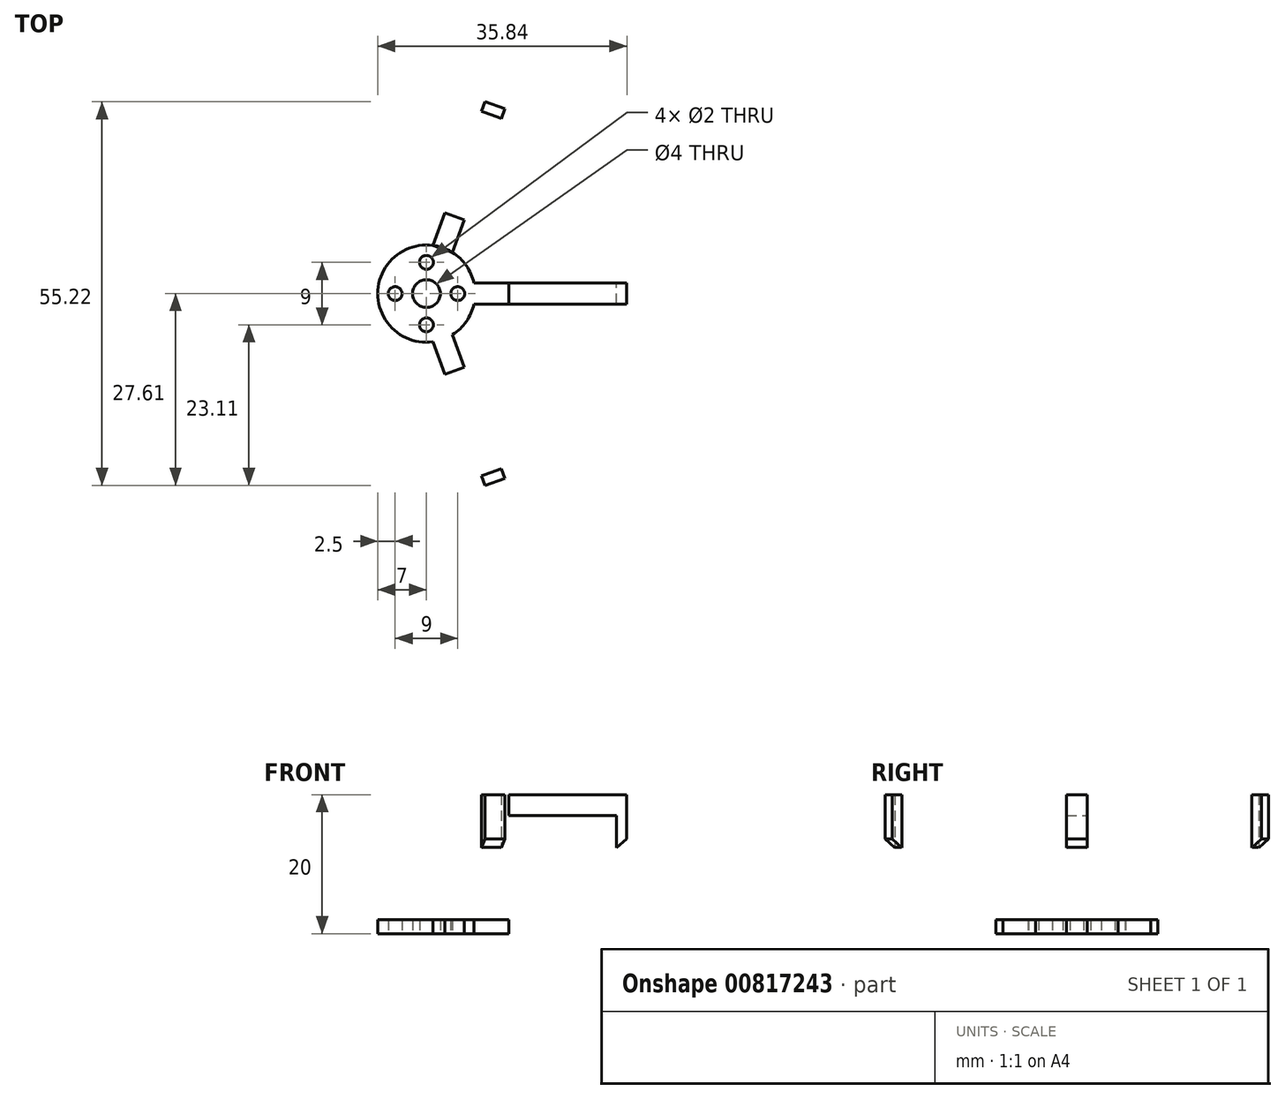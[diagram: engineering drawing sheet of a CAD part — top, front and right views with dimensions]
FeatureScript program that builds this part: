
annotation { "Feature Type Name" : "Feature", "Feature Type Description" : "" }
export const myFeature = defineFeature(function(context is Context, id is Id, definition is map)
    precondition{}
    {
        {
            var Q0;
            Q0=qCreatedBy(makeId("Top.planeOp"),FACE);
            var sketch = newSketch(context, id + "F0", { "sketchPlane" : qUnion([Q0])});
            skCircle(sketch, "E0", {"center": v(0, 0) * mm, "radius": 7 * mm});
            skCircle(sketch, "E1", {"center": v(0, -4.5) * mm, "radius": 1 * mm});
            skCircle(sketch, "E2.1.0", {"center": v(4.5, 0) * mm, "radius": 1 * mm});
            skCircle(sketch, "E2.2.0", {"center": v(0, 4.5) * mm, "radius": 1 * mm});
            skCircle(sketch, "E2.3.0", {"center": v(-4.5, 0) * mm, "radius": 1 * mm});
            skLineSegment(sketch, "E3.bottom", {"start": v(6.84, -1.5) * mm, "end": v(11.84, -1.5) * mm});
            skLineSegment(sketch, "E3.top", {"start": v(6.84, 1.5) * mm, "end": v(11.84, 1.5) * mm});
            skLineSegment(sketch, "E3.left", {"start": v(6.84, -1.5) * mm, "end": v(6.84, 1.5) * mm});
            skLineSegment(sketch, "E3.right", {"start": v(11.84, -1.5) * mm, "end": v(11.84, 1.5) * mm});
            skCircle(sketch, "E4", {"center": v(0, 0) * mm, "radius": 2 * mm});
            skLineSegment(sketch, "E5.1.0", {"start": v(0.93, -6.94) * mm, "end": v(3.75, -5.91) * mm});
            skLineSegment(sketch, "E5.1.1", {"start": v(0.93, -6.94) * mm, "end": v(2.64, -11.64) * mm});
            skLineSegment(sketch, "E5.1.2", {"start": v(3.75, -5.91) * mm, "end": v(5.46, -10.61) * mm});
            skLineSegment(sketch, "E5.1.3", {"start": v(2.64, -11.64) * mm, "end": v(5.46, -10.61) * mm});
            skLineSegment(sketch, "E5.anchor1", {"start": v(0, 0) * mm, "end": v(6.84, -1.5) * mm, "construction": true});
            skLineSegment(sketch, "E5.anchor2", {"start": v(0, 0) * mm, "end": v(0.93, -6.94) * mm, "construction": true});
            skLineSegment(sketch, "E6.MirrorCS", {"start": v(3.75, 5.91) * mm, "end": v(5.46, 10.61) * mm});
            skLineSegment(sketch, "E7.MirrorCS", {"start": v(0.93, 6.94) * mm, "end": v(2.64, 11.64) * mm});
            skLineSegment(sketch, "E8.MirrorCS", {"start": v(0.93, 6.94) * mm, "end": v(3.75, 5.91) * mm});
            skLineSegment(sketch, "E9.MirrorCS", {"start": v(2.64, 11.64) * mm, "end": v(5.46, 10.61) * mm});
            skPoint(sketch, "E10", {"position": v(11.84, 0) * mm});
            skLineSegment(sketch, "E11.bottom", {"start": v(11.84, -1.5) * mm, "end": v(28.84, -1.5) * mm});
            skLineSegment(sketch, "E11.top", {"start": v(11.84, 1.5) * mm, "end": v(28.84, 1.5) * mm});
            skLineSegment(sketch, "E11.right", {"start": v(28.84, -1.5) * mm, "end": v(28.84, 1.5) * mm});
            skLineSegment(sketch, "E12.1.1", {"start": v(8.45, -27.61) * mm, "end": v(11.27, -26.59) * mm});
            skLineSegment(sketch, "E12.1.2", {"start": v(2.64, -11.64) * mm, "end": v(8.45, -27.61) * mm});
            skLineSegment(sketch, "E12.1.3", {"start": v(5.46, -10.61) * mm, "end": v(11.27, -26.59) * mm});
            skLineSegment(sketch, "E12.anchor1", {"start": v(0, 0) * mm, "end": v(16.77, -2.13) * mm, "construction": true});
            skLineSegment(sketch, "E12.anchor2", {"start": v(0, 0) * mm, "end": v(2.64, -11.64) * mm, "construction": true});
            skLineSegment(sketch, "E13.MirrorCS", {"start": v(2.64, 11.64) * mm, "end": v(8.45, 27.61) * mm});
            skLineSegment(sketch, "E14.MirrorCS", {"start": v(8.45, 27.61) * mm, "end": v(11.27, 26.59) * mm});
            skLineSegment(sketch, "E15.MirrorCS", {"start": v(5.46, 10.61) * mm, "end": v(11.27, 26.59) * mm});
            skArc(sketch, "E16", {"start": v(8.45, 27.61) * mm, "mid": v(28.88, 0) * mm, "end": v(8.45, -27.61) * mm});
            skArc(sketch, "E17", {"start": v(7.94, 26.2) * mm, "mid": v(27.38, 0) * mm, "end": v(7.94, -26.2) * mm});
            skPoint(sketch, "E18", {"position": v(6.84, 0) * mm});
            skLineSegment(sketch, "E19.anchor1", {"start": v(0, 0) * mm, "end": v(11.4, 1.92) * mm, "construction": true});
            skLineSegment(sketch, "E19.anchor2", {"start": v(0, 0) * mm, "end": v(5.7, -10.06) * mm, "construction": true});
            skSolve(sketch);
        }
        {
            var Q0;
            {var subQ5=sQuery(id+"F0.wireOp",EDGE,"E8.MirrorCS");Q0=makeQuery(id+"F0.imprint","IMPRINT",FACE,{"disambiguationData":[TD([[makeQuery(id+"F0.imprint","IMPRINT",EDGE,{"derivedFrom":subQ5}),1.0]])]});}
            var Q1;
            Q1=makeQuery(id+"F0.imprint","IMPRINT",FACE,{"disambiguationData":[TD([[makeQuery(id+"F0.imprint","IMPRINT",EDGE,{"derivedFrom":sQuery(id+"F0.wireOp",EDGE,"E1")}),-1.0]])]});
            var Q2;
            {var subQ1=sQuery(id+"F0.wireOp",EDGE,"E3.bottom");Q2=makeQuery(id+"F0.imprint","IMPRINT",FACE,{"disambiguationData":[TD([[makeQuery(id+"F0.imprint","IMPRINT",EDGE,{"derivedFrom":subQ1}),1.0]])]});}
            var Q3;
            {var subQ0=sQuery(id+"F0.wireOp",EDGE,"E3.left");Q3=makeQuery(id+"F0.imprint","IMPRINT",FACE,{"disambiguationData":[TD([[makeQuery(id+"F0.imprint","IMPRINT",EDGE,{"derivedFrom":subQ0}),-1.0]])]});}
            var Q4;
            {var subQ0=sQuery(id+"F0.wireOp",EDGE,"E5.1.0");Q4=makeQuery(id+"F0.imprint","IMPRINT",FACE,{"disambiguationData":[TD([[makeQuery(id+"F0.imprint","IMPRINT",EDGE,{"derivedFrom":subQ0}),-1.0]])]});}
            var Q5;
            {var subQ0=sQuery(id+"F0.wireOp",EDGE,"E5.1.1");Q5=makeQuery(id+"F0.imprint","IMPRINT",FACE,{"disambiguationData":[TD([[makeQuery(id+"F0.imprint","IMPRINT",EDGE,{"derivedFrom":subQ0}),1.0]])]});}
            var Q6;
            {var subQ1=sQuery(id+"F0.wireOp",EDGE,"E6.MirrorCS");Q6=makeQuery(id+"F0.imprint","IMPRINT",FACE,{"disambiguationData":[TD([[makeQuery(id+"F0.imprint","IMPRINT",EDGE,{"derivedFrom":subQ1}),1.0]])]});}
            extrude(context, id + "F1", {"entities" : qUnion([Q0, Q1, Q2, Q3, Q4, Q5, Q6]), "depth" : 2 * mm, "offsetDistance" : 25 * mm});
        }
        {
            var Q0;
            {var subQ1=sQuery(id+"F0.wireOp",EDGE,"E11.bottom");var subQ3=sQuery(id+"F0.wireOp",EDGE,"E17");var subQ4=makeQuery(id+"F0.imprint","INTERSECT",VERTEX,{"derivedFrom":[subQ1,subQ3]});Q0=makeQuery(id+"F0.imprint","IMPRINT",FACE,{"disambiguationData":[TD([[makeQuery(id+"F0.imprint","IMPRINT",EDGE,{"disambiguationData":[TD([[subQ4,-1.0]])],"derivedFrom":subQ3}),1.0]])]});}
            var Q1;
            {var subQ0=sQuery(id+"F0.wireOp",EDGE,"E12.1.1");Q1=makeQuery(id+"F0.imprint","IMPRINT",FACE,{"disambiguationData":[TD([[makeQuery(id+"F0.imprint","IMPRINT",EDGE,{"derivedFrom":subQ0}),1.0]])]});}
            var Q2;
            {var subQ1=sQuery(id+"F0.wireOp",EDGE,"E11.top");var subQ3=sQuery(id+"F0.wireOp",EDGE,"E17");var subQ4=makeQuery(id+"F0.imprint","INTERSECT",VERTEX,{"derivedFrom":[subQ1,subQ3]});Q2=makeQuery(id+"F0.imprint","IMPRINT",FACE,{"disambiguationData":[TD([[makeQuery(id+"F0.imprint","IMPRINT",EDGE,{"disambiguationData":[TD([[subQ4,1.0]])],"derivedFrom":subQ3}),1.0]])]});}
            var Q3;
            {var subQ1=sQuery(id+"F0.wireOp",EDGE,"E14.MirrorCS");Q3=makeQuery(id+"F0.imprint","IMPRINT",FACE,{"disambiguationData":[TD([[makeQuery(id+"F0.imprint","IMPRINT",EDGE,{"derivedFrom":subQ1}),-1.0]])]});}
            var Q4;
            {var subQ1=sQuery(id+"F0.wireOp",EDGE,"E11.right");Q4=makeQuery(id+"F0.imprint","IMPRINT",FACE,{"disambiguationData":[TD([[makeQuery(id+"F0.imprint","IMPRINT",EDGE,{"derivedFrom":subQ1}),1.0]])]});}
            extrude(context, id + "F2", {"entities" : qUnion([Q0, Q1, Q2, Q3, Q4]), "depth" : 20 * mm, "offsetDistance" : 25 * mm, "hasSecondDirection" : true, "secondDirectionOppositeDirection" : true, "secondDirectionDepth" : -17 * mm});
        }
        {
            var Q0;
            {var subQ0=sQuery(id+"F0.wireOp",EDGE,"E5.1.3");Q0=makeQuery(id+"F0.imprint","IMPRINT",FACE,{"disambiguationData":[TD([[makeQuery(id+"F0.imprint","IMPRINT",EDGE,{"derivedFrom":subQ0}),-1.0]])]});}
            var Q1;
            {var subQ1=sQuery(id+"F0.wireOp",EDGE,"E14.MirrorCS");Q1=makeQuery(id+"F0.imprint","IMPRINT",FACE,{"disambiguationData":[TD([[makeQuery(id+"F0.imprint","IMPRINT",EDGE,{"derivedFrom":subQ1}),-1.0]])]});}
            var Q2;
            {var subQ1=sQuery(id+"F0.wireOp",EDGE,"E11.right");Q2=makeQuery(id+"F0.imprint","IMPRINT",FACE,{"disambiguationData":[TD([[makeQuery(id+"F0.imprint","IMPRINT",EDGE,{"derivedFrom":subQ1}),1.0]])]});}
            var Q3;
            {var subQ0=sQuery(id+"F0.wireOp",EDGE,"E12.1.1");Q3=makeQuery(id+"F0.imprint","IMPRINT",FACE,{"disambiguationData":[TD([[makeQuery(id+"F0.imprint","IMPRINT",EDGE,{"derivedFrom":subQ0}),1.0]])]});}
            var Q4;
            {var subQ0=sQuery(id+"F0.wireOp",EDGE,"E3.right");Q4=makeQuery(id+"F0.imprint","IMPRINT",FACE,{"disambiguationData":[TD([[makeQuery(id+"F0.imprint","IMPRINT",EDGE,{"derivedFrom":subQ0}),-1.0]])]});}
            var Q5;
            {var subQ0=sQuery(id+"F0.wireOp",EDGE,"E9.MirrorCS");Q5=makeQuery(id+"F0.imprint","IMPRINT",FACE,{"disambiguationData":[TD([[makeQuery(id+"F0.imprint","IMPRINT",EDGE,{"derivedFrom":subQ0}),1.0]])]});}
            extrude(context, id + "F3", {"entities" : qUnion([Q0, Q1, Q2, Q3, Q4, Q5]), "operationType" : NewBodyOperationType.ADD, "depth" : 20 * mm, "offsetDistance" : 25 * mm});
        }
        {
            var Q0;
            {var subQ0=sQuery(id+"F0.wireOp",EDGE,"E12.1.2");Q0=makeQuery(id+"F3.boolean.opBoolean","MERGE",FACE,{"derivedFrom":[makeQuery(id+"F2.opExtrude","SWEPT_FACE",FACE,{"disambiguationData":[OSD([subQ0])]}),makeQuery(id+"F3.opExtrude","SWEPT_FACE",FACE,{"disambiguationData":[OSD([subQ0])]})]});}
            var sketch = newSketch(context, id + "F4", { "sketchPlane" : qUnion([Q0])});
            skLineSegment(sketch, "E20", {"start": v(28.84, 20) * mm, "end": v(28.84, 13.65) * mm});
            skLineSegment(sketch, "E21", {"start": v(28.84, 13.65) * mm, "end": v(12.57, 0) * mm});
            skLineSegment(sketch, "E22", {"start": v(28.84, 20) * mm, "end": v(27.34, 20) * mm});
            skLineSegment(sketch, "E23", {"start": v(27.34, 20) * mm, "end": v(27.34, 15) * mm});
            skLineSegment(sketch, "E24", {"start": v(11.84, 2) * mm, "end": v(27.34, 15) * mm});
            skLineSegment(sketch, "E25", {"start": v(11.84, 2) * mm, "end": v(11.84, 0) * mm});
            skLineSegment(sketch, "E26", {"start": v(11.84, 0) * mm, "end": v(12.57, 0) * mm});
            skSolve(sketch);
        }
        {
            var Q0;
            {var subQ0=sQuery(id+"F4.wireOp",EDGE,"E23");Q0=makeQuery(id+"F4.imprint","IMPRINT",FACE,{"disambiguationData":[TD([[makeQuery(id+"F4.imprint","IMPRINT",EDGE,{"derivedFrom":subQ0}),-1.0]])]});}
            var Q1;
            {var subQ0=sQuery(id+"F4.wireOp",EDGE,"E21");Q1=makeQuery(id+"F4.imprint","IMPRINT",FACE,{"disambiguationData":[TD([[makeQuery(id+"F4.imprint","IMPRINT",EDGE,{"derivedFrom":subQ0}),1.0]])]});}
            extrude(context, id + "F5", {"entities" : qUnion([Q0, Q1]), "operationType" : NewBodyOperationType.REMOVE, "oppositeDirection" : true, "depth" : 3 * mm, "offsetDistance" : 25 * mm});
        }
        {
            var Q0;
            Q0=makeQuery(id+"F3.opExtrude","SWEPT_FACE",FACE,{"disambiguationData":[OSD([sQuery(id+"F0.wireOp",EDGE,"E11.bottom")])]});
            var sketch = newSketch(context, id + "F6", { "sketchPlane" : qUnion([Q0])});
            skLineSegment(sketch, "E27", {"start": v(28.84, 20) * mm, "end": v(28.84, 13.65) * mm});
            skLineSegment(sketch, "E28", {"start": v(28.84, 13.65) * mm, "end": v(12.57, 0) * mm});
            skLineSegment(sketch, "E29", {"start": v(28.84, 20) * mm, "end": v(27.34, 20) * mm});
            skLineSegment(sketch, "E30", {"start": v(27.34, 20) * mm, "end": v(27.34, 15) * mm});
            skLineSegment(sketch, "E31", {"start": v(11.84, 2) * mm, "end": v(27.34, 15) * mm});
            skLineSegment(sketch, "E32", {"start": v(11.84, 2) * mm, "end": v(11.84, 0) * mm});
            skLineSegment(sketch, "E33", {"start": v(11.84, 0) * mm, "end": v(12.57, 0) * mm});
            skSolve(sketch);
        }
        {
            var Q0;
            Q0=makeQuery(id+"F3.opExtrude","SWEPT_FACE",FACE,{"disambiguationData":[OSD([sQuery(id+"F0.wireOp",EDGE,"E15.MirrorCS")])]});
            var sketch = newSketch(context, id + "F7", { "sketchPlane" : qUnion([Q0])});
            skLineSegment(sketch, "E34", {"start": v(28.84, 20) * mm, "end": v(28.84, 13.65) * mm});
            skLineSegment(sketch, "E35", {"start": v(28.84, 13.65) * mm, "end": v(12.57, 0) * mm});
            skLineSegment(sketch, "E36", {"start": v(28.84, 20) * mm, "end": v(27.34, 20) * mm});
            skLineSegment(sketch, "E37", {"start": v(27.34, 20) * mm, "end": v(27.34, 15) * mm});
            skLineSegment(sketch, "E38", {"start": v(11.84, 2) * mm, "end": v(27.34, 15) * mm});
            skLineSegment(sketch, "E39", {"start": v(11.84, 2) * mm, "end": v(11.84, 0) * mm});
            skLineSegment(sketch, "E40", {"start": v(11.84, 0) * mm, "end": v(12.57, 0) * mm});
            skSolve(sketch);
        }
        {
            var Q0;
            {var subQ0=sQuery(id+"F6.wireOp",EDGE,"E28");Q0=makeQuery(id+"F6.imprint","IMPRINT",FACE,{"disambiguationData":[TD([[makeQuery(id+"F6.imprint","IMPRINT",EDGE,{"derivedFrom":subQ0}),1.0]])]});}
            var Q1;
            {var subQ0=sQuery(id+"F6.wireOp",EDGE,"E31");Q1=makeQuery(id+"F6.imprint","IMPRINT",FACE,{"disambiguationData":[TD([[makeQuery(id+"F6.imprint","IMPRINT",EDGE,{"derivedFrom":subQ0}),1.0]])]});}
            extrude(context, id + "F8", {"entities" : qUnion([Q0, Q1]), "operationType" : NewBodyOperationType.REMOVE, "oppositeDirection" : true, "depth" : 3 * mm, "offsetDistance" : 25 * mm});
        }
        {
            var Q0;
            {var subQ0=sQuery(id+"F7.wireOp",EDGE,"E38");Q0=makeQuery(id+"F7.imprint","IMPRINT",FACE,{"disambiguationData":[TD([[makeQuery(id+"F7.imprint","IMPRINT",EDGE,{"derivedFrom":subQ0}),1.0]])]});}
            var Q1;
            {var subQ0=sQuery(id+"F7.wireOp",EDGE,"E35");Q1=makeQuery(id+"F7.imprint","IMPRINT",FACE,{"disambiguationData":[TD([[makeQuery(id+"F7.imprint","IMPRINT",EDGE,{"derivedFrom":subQ0}),1.0]])]});}
            extrude(context, id + "F9", {"entities" : qUnion([Q0, Q1]), "operationType" : NewBodyOperationType.REMOVE, "oppositeDirection" : true, "depth" : 3 * mm, "offsetDistance" : 25 * mm});
        }
    });
